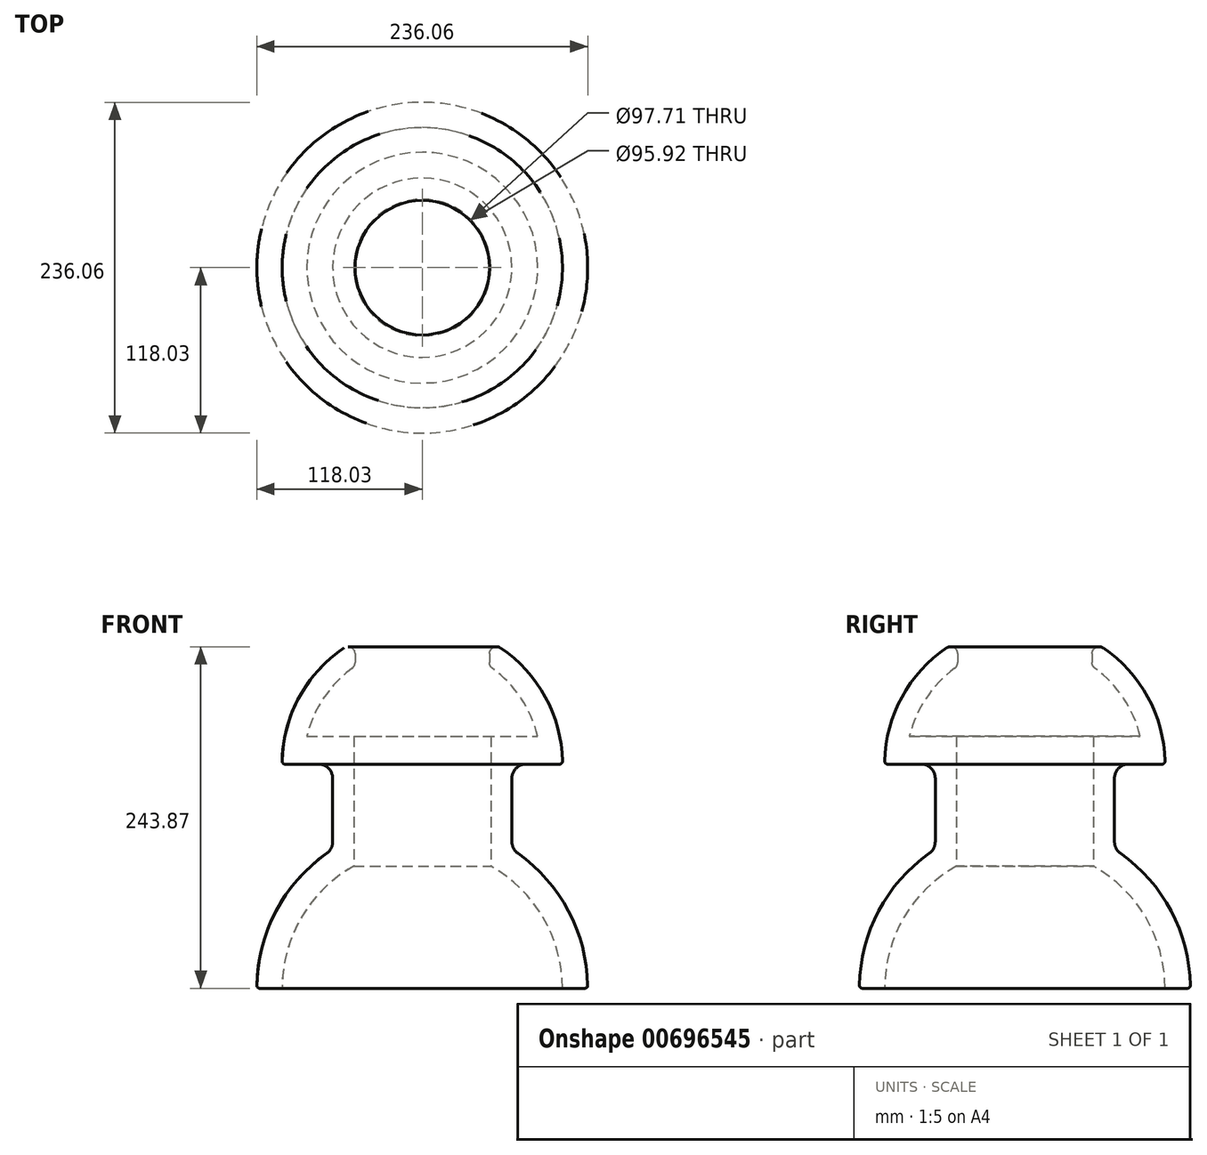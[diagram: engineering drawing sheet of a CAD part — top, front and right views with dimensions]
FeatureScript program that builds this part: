
annotation { "Feature Type Name" : "Feature", "Feature Type Description" : "" }
export const myFeature = defineFeature(function(context is Context, id is Id, definition is map)
    precondition{}
    {
        {
            var Q0;
            Q0=qCreatedBy(makeId("Front.planeOp"),FACE);
            var sketch = newSketch(context, id + "F0", { "sketchPlane" : qUnion([Q0])});
            skArc(sketch, "E0", {"start": v(100, 0) * mm, "mid": v(86.27, 50.57) * mm, "end": v(48.85, 87.25) * mm});
            skPoint(sketch, "E1.orphan", {"position": v(-100, 0) * mm});
            skPoint(sketch, "E2.end.orphan", {"position": v(0, 360.63) * mm});
            skArc(sketch, "E3", {"start": v(100, 160) * mm, "mid": v(70.71, 230.71) * mm, "end": v(0, 260) * mm});
            skArc(sketch, "E4", {"start": v(82.4, 179.88) * mm, "mid": v(52.44, 226.6) * mm, "end": v(0, 244.76) * mm});
            skArc(sketch, "E5", {"start": v(118.04, 0) * mm, "mid": v(103.64, 56.5) * mm, "end": v(63.96, 99.21) * mm});
            skLineSegment(sketch, "E6", {"start": v(63.96, 160) * mm, "end": v(63.96, 99.21) * mm});
            skLineSegment(sketch, "E7", {"start": v(48.85, 87.25) * mm, "end": v(48.85, 179.88) * mm});
            skPoint(sketch, "E8.orphan", {"position": v(84.76, 179.88) * mm});
            skPoint(sketch, "E9.orphan", {"position": v(84.76, 160) * mm});
            skLineSegment(sketch, "E10", {"start": v(82.4, 179.88) * mm, "end": v(48.85, 179.88) * mm});
            skLineSegment(sketch, "E11", {"start": v(63.96, 160) * mm, "end": v(100, 160) * mm});
            skLineSegment(sketch, "E12", {"start": v(0, 260) * mm, "end": v(0, 244.76) * mm});
            skLineSegment(sketch, "E13", {"start": v(100, 0) * mm, "end": v(118.04, 0) * mm});
            skLineSegment(sketch, "E14", {"start": v(0, 0) * mm, "end": v(0, 160) * mm});
            skSolve(sketch);
        }
        {
            var Q0;
            Q0=makeQuery(id+"F0.imprint","IMPRINT",FACE,{"disambiguationData":[TD([[makeQuery(id+"F0.imprint","IMPRINT",EDGE,{"derivedFrom":sQuery(id+"F0.wireOp",EDGE,"E0")}),-1.0]])]});
            var Q1;
            Q1=sQuery(id+"F0.wireOp",EDGE,"E14");
            revolve(context, id + "F1", {"entities" : qUnion([Q0]), "axis" : qUnion([Q1]), "revolveType" : RevolveType.FULL});
        }
        {
            var Q0;
            Q0=qCreatedBy(makeId("Top.planeOp"),FACE);
            var sketch = newSketch(context, id + "F2", { "sketchPlane" : qUnion([Q0])});
            skCircle(sketch, "E15", {"center": v(0, 0) * mm, "radius": 47.96 * mm});
            skSolve(sketch);
        }
        {
            var Q0;
            Q0=makeQuery(id+"F2.imprint","IMPRINT",FACE,{"disambiguationData":[TD([[makeQuery(id+"F2.imprint","IMPRINT",EDGE,{"derivedFrom":sQuery(id+"F2.wireOp",EDGE,"E15")}),1.0]])]});
            extrude(context, id + "F3", {"entities" : qUnion([Q0]), "operationType" : NewBodyOperationType.REMOVE, "depth" : 261 * mm, "offsetDistance" : 25 * mm});
        }
        {
            var Q0;
            Q0=makeQuery(id+"F1.opRevolve","SWEPT_EDGE",EDGE,{"disambiguationData":[OSD([sQuery(id+"F0.wireOp",EDGE,"E6"),sQuery(id+"F0.wireOp",EDGE,"E11")])]});
            var Q1;
            Q1=makeQuery(id+"F1.opRevolve","SWEPT_EDGE",EDGE,{"disambiguationData":[OSD([sQuery(id+"F0.wireOp",EDGE,"E5"),sQuery(id+"F0.wireOp",EDGE,"E6")])]});
            fillet(context, id + "F4", {"entities" : qUnion([Q0, Q1]), "radius" : 10 * mm, "tangentPropagation" : true, "allowEdgeOverflow" : false});
        }
        {
            var Q0;
            Q0=makeQuery(id+"F1.opRevolve","SWEPT_EDGE",EDGE,{"disambiguationData":[OSD([sQuery(id+"F0.wireOp",EDGE,"E3"),sQuery(id+"F0.wireOp",EDGE,"E11")])]});
            var Q1;
            Q1=makeQuery(id+"F1.opRevolve","SWEPT_EDGE",EDGE,{"disambiguationData":[OSD([sQuery(id+"F0.wireOp",EDGE,"E5"),sQuery(id+"F0.wireOp",EDGE,"E13")])]});
            fillet(context, id + "F5", {"entities" : qUnion([Q0, Q1]), "radius" : 2 * mm, "tangentPropagation" : true, "allowEdgeOverflow" : false});
        }
        {
            var Q0;
            Q0=makeQuery(id+"F3.boolean.opBoolean","INTERSECT",EDGE,{"derivedFrom":[makeQuery(id+"F1.opRevolve","SWEPT_FACE",FACE,{"disambiguationData":[OSD([sQuery(id+"F0.wireOp",EDGE,"E4")])]}),makeQuery(id+"F3.opExtrude","SWEPT_FACE",FACE,{"disambiguationData":[OSD([sQuery(id+"F2.wireOp",EDGE,"E15")])]})]});
            var Q1;
            Q1=makeQuery(id+"F3.boolean.opBoolean","INTERSECT",EDGE,{"derivedFrom":[makeQuery(id+"F1.opRevolve","SWEPT_FACE",FACE,{"disambiguationData":[OSD([sQuery(id+"F0.wireOp",EDGE,"E3")])]}),makeQuery(id+"F3.opExtrude","SWEPT_FACE",FACE,{"disambiguationData":[OSD([sQuery(id+"F2.wireOp",EDGE,"E15")])]})]});
            fillet(context, id + "F6", {"entities" : qUnion([Q0, Q1]), "radius" : 5 * mm, "tangentPropagation" : true, "allowEdgeOverflow" : false});
        }
    });
